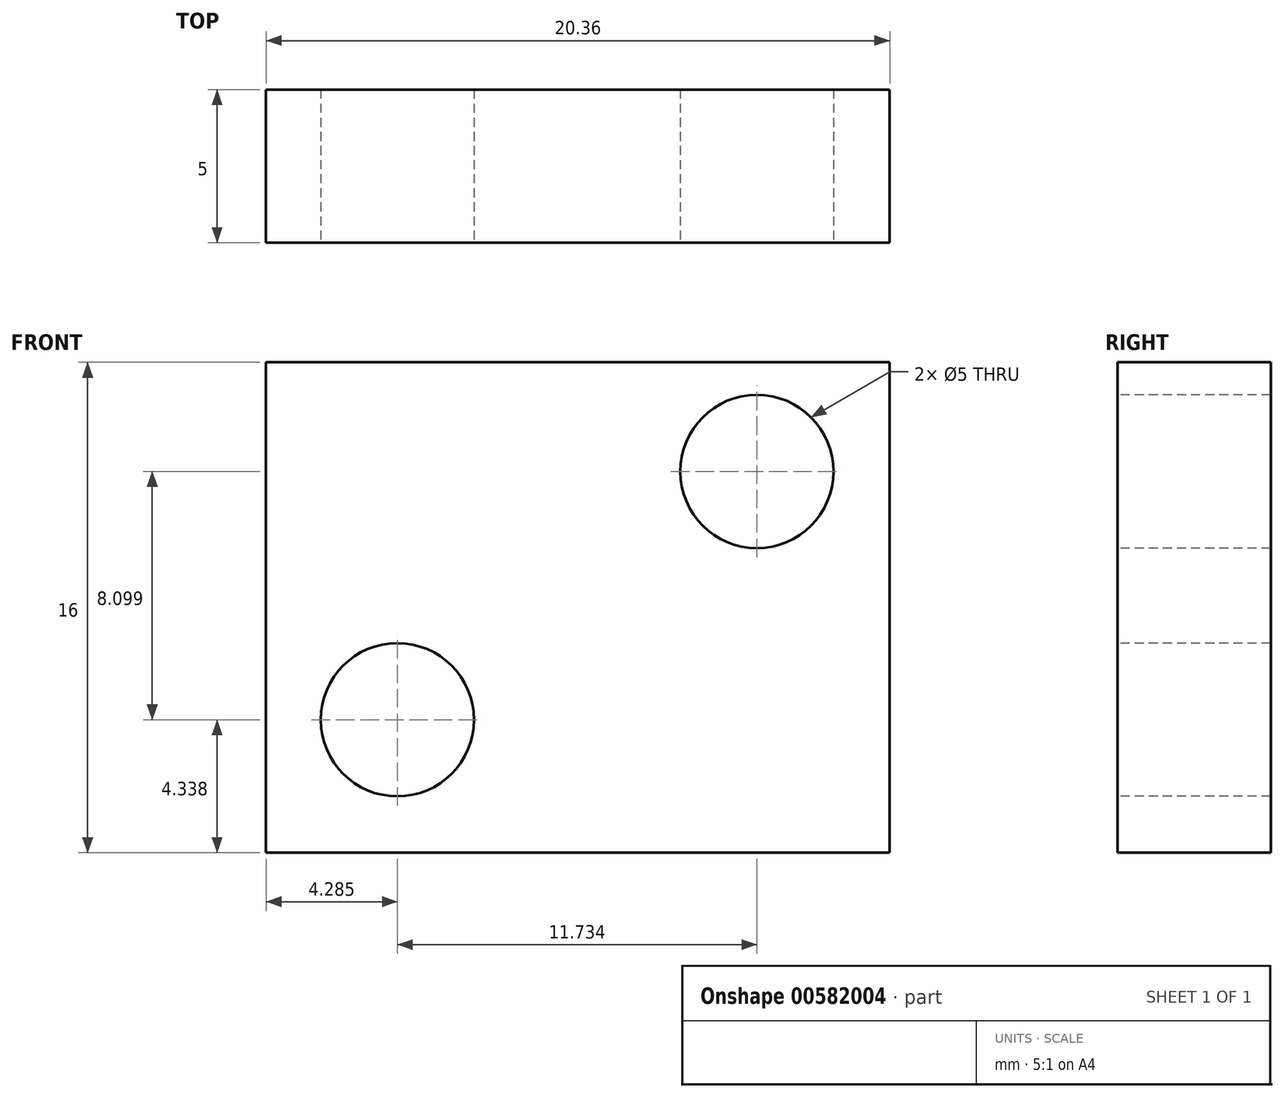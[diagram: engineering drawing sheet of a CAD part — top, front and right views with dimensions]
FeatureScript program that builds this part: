
annotation { "Feature Type Name" : "Feature", "Feature Type Description" : "" }
export const myFeature = defineFeature(function(context is Context, id is Id, definition is map)
    precondition{}
    {
        {
            var Q0;
            Q0=qCreatedBy(makeId("Front.planeOp"),FACE);
            var sketch = newSketch(context, id + "F0", { "sketchPlane" : qUnion([Q0])});
            skLineSegment(sketch, "E0", {"start": v(-12.04, 9.83) * mm, "end": v(8.32, 9.83) * mm});
            skLineSegment(sketch, "E1", {"start": v(8.32, 9.83) * mm, "end": v(8.32, -6.17) * mm});
            skLineSegment(sketch, "E2", {"start": v(8.32, -6.17) * mm, "end": v(-12.04, -6.17) * mm});
            skLineSegment(sketch, "E3", {"start": v(-12.04, -6.17) * mm, "end": v(-12.04, 9.83) * mm});
            skSolve(sketch);
        }
        {
            var Q0;
            Q0 = qSketchRegion(id + "F0", true);
            extrude(context, id + "F1", {"entities" : qUnion([Q0]), "depth" : 5 * mm, "offsetDistance" : 25 * mm});
        }
        {
            var Q0;
            Q0=makeQuery(id+"F1.opExtrude","CAP_FACE",FACE,{"disambiguationData":[OSD([sQuery(id+"F0.wireOp",EDGE,"E0"),sQuery(id+"F0.wireOp",EDGE,"E1"),sQuery(id+"F0.wireOp",EDGE,"E2"),sQuery(id+"F0.wireOp",EDGE,"E3")])],"isStart":false});
            var sketch = newSketch(context, id + "F2", { "sketchPlane" : qUnion([Q0])});
            skCircle(sketch, "E4", {"center": v(-7.75, -1.83) * mm, "radius": 2.5 * mm});
            skSolve(sketch);
        }
        {
            var Q0;
            Q0=makeQuery(id+"F2.imprint","IMPRINT",FACE,{"disambiguationData":[TD([[makeQuery(id+"F2.imprint","IMPRINT",EDGE,{"derivedFrom":sQuery(id+"F2.wireOp",EDGE,"E4")}),1.0]])]});
            extrude(context, id + "F3", {"entities" : qUnion([Q0]), "operationType" : NewBodyOperationType.REMOVE, "endBound" : BoundingType.THROUGH_ALL, "oppositeDirection" : true, "depth" : 25 * mm, "offsetDistance" : 25 * mm});
        }
        {
            var Q0;
            Q0=makeQuery(id+"F1.opExtrude","CAP_FACE",FACE,{"disambiguationData":[OSD([sQuery(id+"F0.wireOp",EDGE,"E0"),sQuery(id+"F0.wireOp",EDGE,"E1"),sQuery(id+"F0.wireOp",EDGE,"E2"),sQuery(id+"F0.wireOp",EDGE,"E3")])],"isStart":false});
            var sketch = newSketch(context, id + "F4", { "sketchPlane" : qUnion([Q0])});
            skCircle(sketch, "E5", {"center": v(3.98, 6.27) * mm, "radius": 2.5 * mm});
            skSolve(sketch);
        }
        {
            var Q0;
            Q0=makeQuery(id+"F4.imprint","IMPRINT",FACE,{"disambiguationData":[TD([[makeQuery(id+"F4.imprint","IMPRINT",EDGE,{"derivedFrom":sQuery(id+"F4.wireOp",EDGE,"E5")}),1.0]])]});
            extrude(context, id + "F5", {"entities" : qUnion([Q0]), "operationType" : NewBodyOperationType.REMOVE, "endBound" : BoundingType.THROUGH_ALL, "oppositeDirection" : true, "depth" : 25 * mm, "offsetDistance" : 25 * mm});
        }
    });
